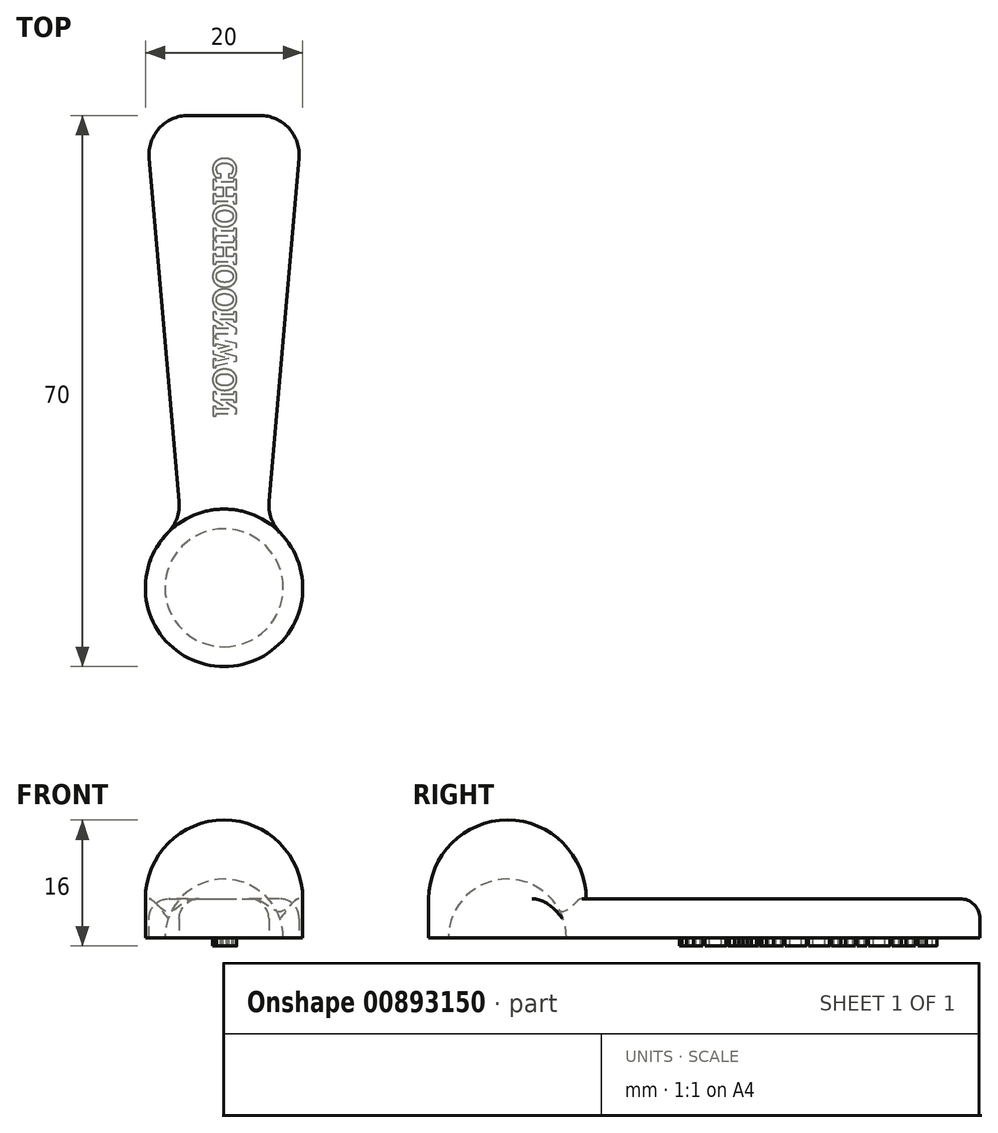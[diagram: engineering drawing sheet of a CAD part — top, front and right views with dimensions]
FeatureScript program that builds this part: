
annotation { "Feature Type Name" : "Feature", "Feature Type Description" : "" }
export const myFeature = defineFeature(function(context is Context, id is Id, definition is map)
    precondition{}
    {
        {
            var Q0;
            Q0=qCreatedBy(makeId("Top.planeOp"),FACE);
            var sketch = newSketch(context, id + "F0", { "sketchPlane" : qUnion([Q0])});
            skCircle(sketch, "E0", {"center": v(0, 0) * mm, "radius": 10 * mm});
            skLineSegment(sketch, "E1", {"start": v(0, 0) * mm, "end": v(0, 60) * mm, "construction": true});
            skLineSegment(sketch, "E2", {"start": v(0, 60) * mm, "end": v(-10, 60) * mm});
            skLineSegment(sketch, "E3", {"start": v(-10, 60) * mm, "end": v(-5.48, 8.36) * mm});
            skLineSegment(sketch, "E4.MirrorCS", {"start": v(10, 60) * mm, "end": v(5.48, 8.36) * mm});
            skLineSegment(sketch, "E5.MirrorCS", {"start": v(0, 60) * mm, "end": v(10, 60) * mm});
            skSolve(sketch);
        }
        {
            var Q0;
            Q0 = qSketchRegion(id + "F0", true);
            extrude(context, id + "F1", {"entities" : qUnion([Q0]), "depth" : 5 * mm, "offsetDistance" : 25 * mm});
        }
        {
            var Q0;
            Q0=makeQuery(id+"F1.opExtrude","CAP_FACE",FACE,{"disambiguationData":[OSD([sQuery(id+"F0.wireOp",EDGE,"E0"),sQuery(id+"F0.wireOp",EDGE,"E2"),sQuery(id+"F0.wireOp",EDGE,"E3"),sQuery(id+"F0.wireOp",EDGE,"E4.MirrorCS"),sQuery(id+"F0.wireOp",EDGE,"E5.MirrorCS")])],"isStart":false});
            var sketch = newSketch(context, id + "F2", { "sketchPlane" : qUnion([Q0])});
            skLineSegment(sketch, "E6", {"start": v(0, 60) * mm, "end": v(0, -10) * mm, "construction": true});
            skSolve(sketch);
        }
        {
            var Q0;
            Q0=makeQuery(id+"F2.imprint","IMPRINT",FACE,{"disambiguationData":[TD([[makeQuery(id+"F2.imprint","IMPRINT",EDGE,{"derivedFrom":makeQuery(id+"F1.opExtrude","CAP_EDGE",EDGE,{"disambiguationData":[OSD([sQuery(id+"F0.wireOp",EDGE,"E0")])],"isStart":false})}),1.0]])]});
            var sketch = newSketch(context, id + "F3", { "sketchPlane" : qUnion([Q0])});
            skArc(sketch, "E7", {"start": v(0, 10) * mm, "mid": v(-10, 0) * mm, "end": v(0, -10) * mm});
            skLineSegment(sketch, "E8", {"start": v(0, 10) * mm, "end": v(0, -10) * mm});
            skSolve(sketch);
        }
        {
            var Q0;
            Q0 = qSketchRegion(id + "F3", true);
            var Q1;
            Q1=sQuery(id+"F2.wireOp",EDGE,"E6");
            revolve(context, id + "F4", {"operationType" : NewBodyOperationType.ADD, "surfaceOperationType" : NewSurfaceOperationType.NEW, "entities" : qUnion([Q0]), "axis" : qUnion([Q1]), "revolveType" : RevolveType.ONE_DIRECTION, "oppositeDirection" : true, "angle" : 180 * degree});
        }
        {
            var Q0;
            Q0=makeQuery(id+"F1.opExtrude","CAP_FACE",FACE,{"disambiguationData":[OSD([sQuery(id+"F0.wireOp",EDGE,"E0"),sQuery(id+"F0.wireOp",EDGE,"E2"),sQuery(id+"F0.wireOp",EDGE,"E3"),sQuery(id+"F0.wireOp",EDGE,"E4.MirrorCS"),sQuery(id+"F0.wireOp",EDGE,"E5.MirrorCS")])],"isStart":true});
            var sketch = newSketch(context, id + "F5", { "sketchPlane" : qUnion([Q0])});
            skCircle(sketch, "E9", {"center": v(0, 0) * mm, "radius": 7.5 * mm});
            skLineSegment(sketch, "E10", {"start": v(0, 7.5) * mm, "end": v(0, -7.5) * mm});
            skPoint(sketch, "E10.startSnap0", {"position": v(0, 10) * mm});
            skSolve(sketch);
        }
        {
            var Q0;
            {var subQ0=sQuery(id+"F5.wireOp",EDGE,"E10");Q0=makeQuery(id+"F5.imprint","IMPRINT",FACE,{"disambiguationData":[TD([[makeQuery(id+"F5.imprint","IMPRINT",EDGE,{"derivedFrom":subQ0}),-1.0]])]});}
            var Q1;
            Q1=sQuery(id+"F5.wireOp",EDGE,"E10");
            revolve(context, id + "F6", {"operationType" : NewBodyOperationType.REMOVE, "surfaceOperationType" : NewSurfaceOperationType.NEW, "entities" : qUnion([Q0]), "axis" : qUnion([Q1]), "revolveType" : RevolveType.FULL, "oppositeDirection" : true});
        }
        {
            var Q0;
            Q0=makeQuery(id+"F1.opExtrude","SWEPT_EDGE",EDGE,{"disambiguationData":[OSD([sQuery(id+"F0.wireOp",EDGE,"E2"),sQuery(id+"F0.wireOp",EDGE,"E3")])]});
            var Q1;
            Q1=makeQuery(id+"F1.opExtrude","SWEPT_EDGE",EDGE,{"disambiguationData":[OSD([sQuery(id+"F0.wireOp",EDGE,"E4.MirrorCS"),sQuery(id+"F0.wireOp",EDGE,"E5.MirrorCS")])]});
            var Q2;
            Q2=makeQuery(id+"F1.opExtrude","SWEPT_EDGE",EDGE,{"disambiguationData":[OSD([sQuery(id+"F0.wireOp",EDGE,"E0"),sQuery(id+"F0.wireOp",EDGE,"E4.MirrorCS")])]});
            var Q3;
            Q3=makeQuery(id+"F1.opExtrude","SWEPT_EDGE",EDGE,{"disambiguationData":[OSD([sQuery(id+"F0.wireOp",EDGE,"E0"),sQuery(id+"F0.wireOp",EDGE,"E3")])]});
            fillet(context, id + "F7", {"entities" : qUnion([Q0, Q1, Q2, Q3]), "radius" : 5 * mm, "tangentPropagation" : true, "allowEdgeOverflow" : false});
        }
        {
            var Q0;
            Q0=makeQuery(id+"F1.opExtrude","CAP_EDGE",EDGE,{"disambiguationData":[OSD([sQuery(id+"F0.wireOp",EDGE,"E3")])],"isStart":false});
            fillet(context, id + "F8", {"entities" : qUnion([Q0]), "radius" : 2.5 * mm, "tangentPropagation" : true, "allowEdgeOverflow" : false});
        }
        {
            var Q0;
            Q0=makeQuery(id+"F1.opExtrude","CAP_FACE",FACE,{"disambiguationData":[OSD([sQuery(id+"F0.wireOp",EDGE,"E0"),sQuery(id+"F0.wireOp",EDGE,"E2"),sQuery(id+"F0.wireOp",EDGE,"E3"),sQuery(id+"F0.wireOp",EDGE,"E4.MirrorCS"),sQuery(id+"F0.wireOp",EDGE,"E5.MirrorCS")])],"isStart":true});
            var sketch = newSketch(context, id + "F9", { "sketchPlane" : qUnion([Q0])});
            skText(sketch, "E11", { "text": "CHOIHOONWON", "fontName": "RobotoSlab-Bold.ttf"});
            skPoint(sketch, "E11.secondSnap0", {"position": v(4.63, -61.2) * mm});
            const initialGuessF9  = {"E11": [0.00156, -0.05465, 0, 1, 0.003]};
            skSetInitialGuess(sketch, initialGuessF9);
            skSolve(sketch);
        }
        {
            var Q0;
            Q0 = qSketchRegion(id + "F9", true);
            extrude(context, id + "F10", {"entities" : qUnion([Q0]), "operationType" : NewBodyOperationType.ADD, "depth" : 1 * mm, "offsetDistance" : 25 * mm});
        }
    });
